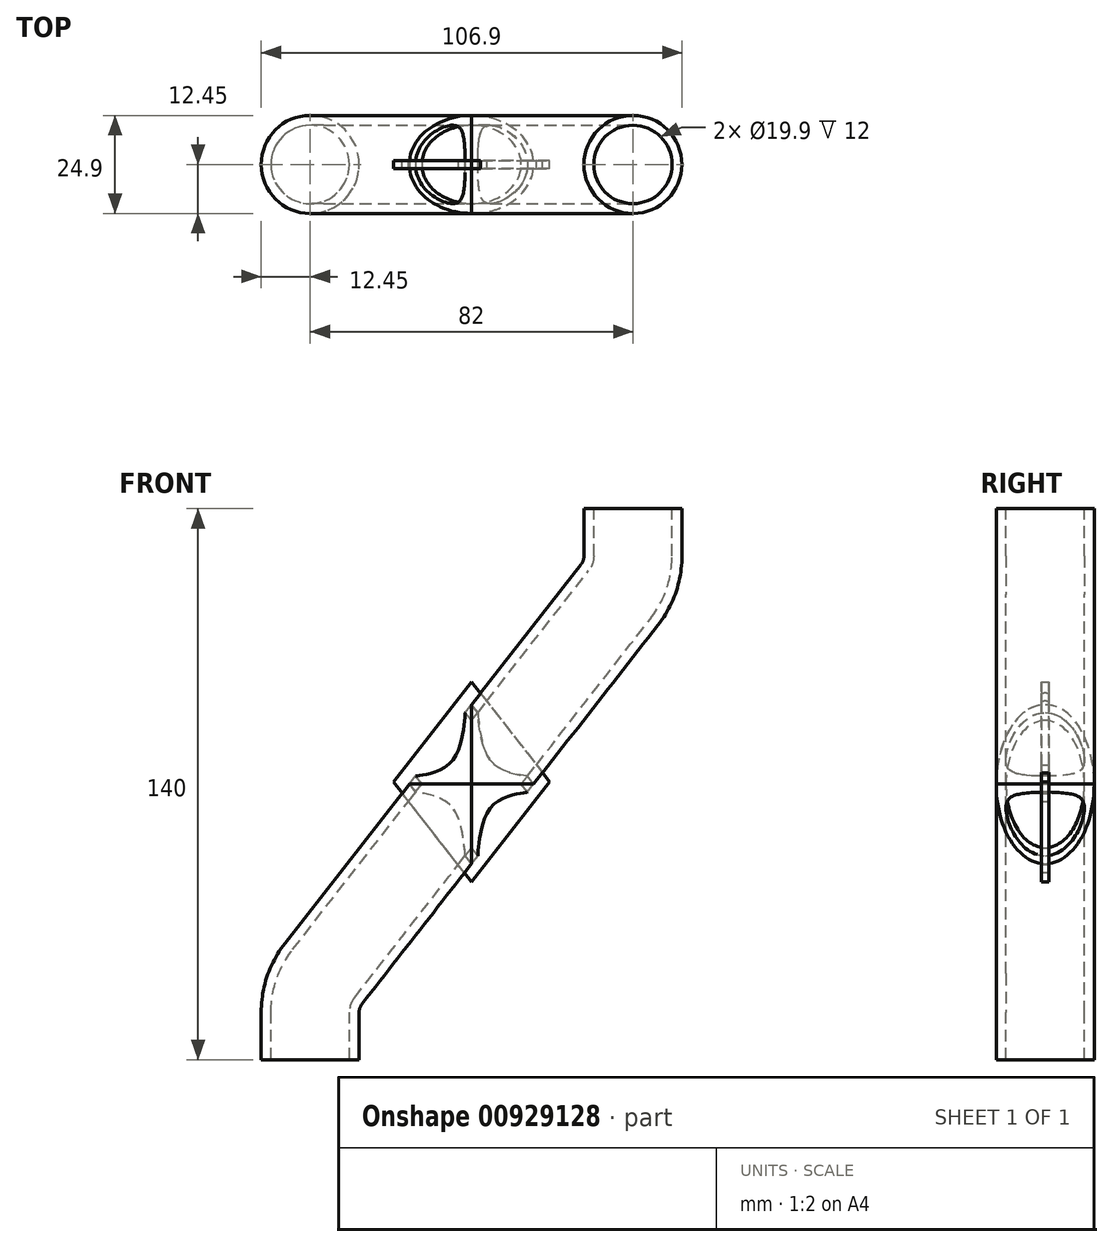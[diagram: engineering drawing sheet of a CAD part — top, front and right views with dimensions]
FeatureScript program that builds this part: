
annotation { "Feature Type Name" : "Feature", "Feature Type Description" : "" }
export const myFeature = defineFeature(function(context is Context, id is Id, definition is map)
    precondition{}
    {
        {
            var Q0;
            Q0=qCreatedBy(makeId("Front.planeOp"),FACE);
            var sketch = newSketch(context, id + "F0", { "sketchPlane" : qUnion([Q0])});
            skLineSegment(sketch, "E0", {"start": v(-41, 0) * mm, "end": v(-41, 12) * mm});
            skLineSegment(sketch, "E1", {"start": v(41, 0) * mm, "end": v(41, 12) * mm});
            skLineSegment(sketch, "E2", {"start": v(-37.6, 21.87) * mm, "end": v(37.6, 118.13) * mm});
            skLineSegment(sketch, "E3", {"start": v(37.6, 21.87) * mm, "end": v(0, 70) * mm});
            skLineSegment(sketch, "E4", {"start": v(-70.89, 0) * mm, "end": v(-70.89, 140) * mm});
            skLineSegment(sketch, "E5", {"start": v(41, 128) * mm, "end": v(41, 140) * mm});
            skPoint(sketch, "E6.visualSharp", {"position": v(-41, 17.52) * mm});
            skArc(sketch, "E6.filletArc", {"start": v(-37.6, 21.87) * mm, "mid": v(-40.13, 17.22) * mm, "end": v(-41, 12) * mm});
            skPoint(sketch, "E7.visualSharp", {"position": v(41, 17.52) * mm});
            skArc(sketch, "E7.filletArc", {"start": v(41, 12) * mm, "mid": v(40.13, 17.22) * mm, "end": v(37.6, 21.87) * mm});
            skPoint(sketch, "E8.visualSharp", {"position": v(41, 122.48) * mm});
            skArc(sketch, "E8.filletArc", {"start": v(37.6, 118.13) * mm, "mid": v(40.13, 122.78) * mm, "end": v(41, 128) * mm});
            skLineSegment(sketch, "E9", {"start": v(0, 70) * mm, "end": v(-15.6, 89.96) * mm});
            skSolve(sketch);
        }
        {
            var Q0;
            Q0=qCreatedBy(makeId("Top.planeOp"),FACE);
            var sketch = newSketch(context, id + "F1", { "sketchPlane" : qUnion([Q0])});
            skPoint(sketch, "E10.0", {"position": v(-41, 0) * mm});
            skCircle(sketch, "E11", {"center": v(-41, 0) * mm, "radius": 12.45 * mm});
            skCircle(sketch, "E12", {"center": v(41, 0) * mm, "radius": 12.45 * mm});
            skSolve(sketch);
        }
        {
            var Q0;
            Q0=makeQuery(id+"F1.imprint","IMPRINT",FACE,{"disambiguationData":[TD([[makeQuery(id+"F1.imprint","IMPRINT",EDGE,{"derivedFrom":sQuery(id+"F1.wireOp",EDGE,"E11")}),1.0]])]});
            var Q1;
            Q1=sQuery(id+"F0.wireOp",EDGE,"E0");
            var Q2;
            Q2=sQuery(id+"F0.wireOp",EDGE,"E6.filletArc");
            var Q3;
            Q3=sQuery(id+"F0.wireOp",EDGE,"E2");
            var Q4;
            Q4=sQuery(id+"F0.wireOp",EDGE,"E8.filletArc");
            var Q5;
            Q5=sQuery(id+"F0.wireOp",EDGE,"E5");
            sweep(context, id + "F2", {"profiles" : qUnion([Q0]), "path" : qUnion([Q1, Q2, Q3, Q4, Q5])});
        }
        {
            var Q0;
            Q0=makeQuery(id+"F1.imprint","IMPRINT",FACE,{"disambiguationData":[TD([[makeQuery(id+"F1.imprint","IMPRINT",EDGE,{"derivedFrom":sQuery(id+"F1.wireOp",EDGE,"E12")}),1.0]])]});
            var Q1;
            Q1=sQuery(id+"F0.wireOp",EDGE,"E1");
            var Q2;
            Q2=sQuery(id+"F0.wireOp",EDGE,"E7.filletArc");
            var Q3;
            Q3=sQuery(id+"F0.wireOp",EDGE,"E3");
            var Q4;
            Q4=sQuery(id+"F0.wireOp",EDGE,"E9");
            sweep(context, id + "F3", {"profiles" : qUnion([Q0]), "path" : qUnion([Q1, Q2, Q3, Q4])});
        }
        {
            var Q0;
            Q0=makeQuery(id+"F3.opSweep","CAP_FACE",FACE,{"disambiguationData":[OSD([sQuery(id+"F0.wireOp",VERTEX,"E9.end"),sQuery(id+"F1.wireOp",EDGE,"E12")])],"isStart":false});
            var Q1;
            Q1=makeQuery(id+"F2.opSweep","CAP_FACE",FACE,{"disambiguationData":[OSD([sQuery(id+"F0.wireOp",VERTEX,"E5.end"),sQuery(id+"F1.wireOp",EDGE,"E11")])],"isStart":false});
            var Q2;
            Q2=makeQuery(id+"F2.opSweep","CAP_FACE",FACE,{"disambiguationData":[OSD([sQuery(id+"F0.wireOp",VERTEX,"E0.start"),sQuery(id+"F1.wireOp",EDGE,"E11")])],"isStart":true});
            var Q3;
            Q3=makeQuery(id+"F3.opSweep","CAP_FACE",FACE,{"disambiguationData":[OSD([sQuery(id+"F0.wireOp",VERTEX,"E1.start"),sQuery(id+"F1.wireOp",EDGE,"E12")])],"isStart":true});
            shell(context, id + "F4", {"entities" : qUnion([Q0, Q1, Q2, Q3]), "thickness" : 2.5 * mm});
        }
        {
            var Q0;
            Q0=qCreatedBy(makeId("Front.planeOp"),FACE);
            var sketch = newSketch(context, id + "F5", { "sketchPlane" : qUnion([Q0])});
            skLineSegment(sketch, "E13", {"start": v(-25.4, 82.3) * mm, "end": v(27.79, 14.2) * mm});
            skLineSegment(sketch, "E14", {"start": v(47.41, 29.54) * mm, "end": v(-5.78, 97.63) * mm});
            skLineSegment(sketch, "E15", {"start": v(27.79, 125.8) * mm, "end": v(-47.41, 29.54) * mm});
            skLineSegment(sketch, "E16", {"start": v(-27.79, 14.2) * mm, "end": v(47.41, 110.46) * mm});
            skLineSegment(sketch, "E17", {"start": v(-19.86, 70.57) * mm, "end": v(0, 96) * mm});
            skLineSegment(sketch, "E18", {"start": v(0, 96) * mm, "end": v(19.86, 70.57) * mm});
            skLineSegment(sketch, "E19", {"start": v(19.86, 70.57) * mm, "end": v(0, 45.15) * mm});
            skLineSegment(sketch, "E20", {"start": v(0, 45.15) * mm, "end": v(-19.86, 70.57) * mm});
            skSolve(sketch);
        }
        {
            var Q0;
            {var subQ0=sQuery(id+"F5.wireOp",EDGE,"E17");var subQ1=sQuery(id+"F5.wireOp",EDGE,"E14");var subQ2=makeQuery(id+"F5.imprint","INTERSECT",VERTEX,{"derivedFrom":[subQ1,subQ0]});Q0=makeQuery(id+"F5.imprint","IMPRINT",FACE,{"disambiguationData":[TD([[makeQuery(id+"F5.imprint","IMPRINT",EDGE,{"disambiguationData":[TD([[subQ2,1.0]])],"derivedFrom":subQ1}),-1.0]])]});}
            var Q1;
            {var subQ0=sQuery(id+"F5.wireOp",EDGE,"E17");var subQ1=sQuery(id+"F5.wireOp",EDGE,"E13");var subQ2=makeQuery(id+"F5.imprint","INTERSECT",VERTEX,{"derivedFrom":[subQ1,subQ0]});Q1=makeQuery(id+"F5.imprint","IMPRINT",FACE,{"disambiguationData":[TD([[makeQuery(id+"F5.imprint","IMPRINT",EDGE,{"disambiguationData":[TD([[subQ2,-1.0]])],"derivedFrom":subQ1}),1.0]])]});}
            var Q2;
            {var subQ0=sQuery(id+"F5.wireOp",EDGE,"E16");var subQ1=sQuery(id+"F5.wireOp",EDGE,"E14");var subQ2=makeQuery(id+"F5.imprint","INTERSECT",VERTEX,{"derivedFrom":[subQ1,subQ0]});Q2=makeQuery(id+"F5.imprint","IMPRINT",FACE,{"disambiguationData":[TD([[makeQuery(id+"F5.imprint","IMPRINT",EDGE,{"disambiguationData":[TD([[subQ2,-1.0]])],"derivedFrom":subQ1}),-1.0]])]});}
            var Q3;
            {var subQ0=sQuery(id+"F5.wireOp",EDGE,"E15");var subQ1=sQuery(id+"F5.wireOp",EDGE,"E13");var subQ2=makeQuery(id+"F5.imprint","INTERSECT",VERTEX,{"derivedFrom":[subQ1,subQ0]});Q3=makeQuery(id+"F5.imprint","IMPRINT",FACE,{"disambiguationData":[TD([[makeQuery(id+"F5.imprint","IMPRINT",EDGE,{"disambiguationData":[TD([[subQ2,-1.0]])],"derivedFrom":subQ1}),1.0]])]});}
            var Q4;
            {var subQ0=sQuery(id+"F5.wireOp",EDGE,"E19");var subQ1=sQuery(id+"F5.wireOp",EDGE,"E14");var subQ2=makeQuery(id+"F5.imprint","INTERSECT",VERTEX,{"derivedFrom":[subQ1,subQ0]});Q4=makeQuery(id+"F5.imprint","IMPRINT",FACE,{"disambiguationData":[TD([[makeQuery(id+"F5.imprint","IMPRINT",EDGE,{"disambiguationData":[TD([[subQ2,-1.0]])],"derivedFrom":subQ1}),-1.0]])]});}
            var Q5;
            {var subQ0=sQuery(id+"F5.wireOp",EDGE,"E19");var subQ1=sQuery(id+"F5.wireOp",EDGE,"E13");var subQ2=makeQuery(id+"F5.imprint","INTERSECT",VERTEX,{"derivedFrom":[subQ1,subQ0]});Q5=makeQuery(id+"F5.imprint","IMPRINT",FACE,{"disambiguationData":[TD([[makeQuery(id+"F5.imprint","IMPRINT",EDGE,{"disambiguationData":[TD([[subQ2,1.0]])],"derivedFrom":subQ1}),1.0]])]});}
            var Q6;
            {var subQ0=sQuery(id+"F5.wireOp",EDGE,"E19");var subQ1=sQuery(id+"F5.wireOp",EDGE,"E13");var subQ2=makeQuery(id+"F5.imprint","INTERSECT",VERTEX,{"derivedFrom":[subQ1,subQ0]});Q6=makeQuery(id+"F5.imprint","IMPRINT",FACE,{"disambiguationData":[TD([[makeQuery(id+"F5.imprint","IMPRINT",EDGE,{"disambiguationData":[TD([[subQ2,1.0]])],"derivedFrom":subQ1}),-1.0]])]});}
            var Q7;
            {var subQ0=sQuery(id+"F5.wireOp",EDGE,"E15");var subQ1=sQuery(id+"F5.wireOp",EDGE,"E13");var subQ2=makeQuery(id+"F5.imprint","INTERSECT",VERTEX,{"derivedFrom":[subQ1,subQ0]});Q7=makeQuery(id+"F5.imprint","IMPRINT",FACE,{"disambiguationData":[TD([[makeQuery(id+"F5.imprint","IMPRINT",EDGE,{"disambiguationData":[TD([[subQ2,-1.0]])],"derivedFrom":subQ1}),-1.0]])]});}
            var Q8;
            {var subQ0=sQuery(id+"F5.wireOp",EDGE,"E17");var subQ1=sQuery(id+"F5.wireOp",EDGE,"E13");var subQ2=makeQuery(id+"F5.imprint","INTERSECT",VERTEX,{"derivedFrom":[subQ1,subQ0]});Q8=makeQuery(id+"F5.imprint","IMPRINT",FACE,{"disambiguationData":[TD([[makeQuery(id+"F5.imprint","IMPRINT",EDGE,{"disambiguationData":[TD([[subQ2,-1.0]])],"derivedFrom":subQ1}),-1.0]])]});}
            extrude(context, id + "F6", {"entities" : qUnion([Q0, Q1, Q2, Q3, Q4, Q5, Q6, Q7, Q8]), "endBound" : BoundingType.SYMMETRIC, "depth" : 2 * mm, "offsetDistance" : 25 * mm});
        }
        {
            var Q0;
            Q0=makeQuery(id+"F2.opSweep","SWEPT_BODY",BODY,{"disambiguationData":[OSD([sQuery(id+"F0.wireOp",EDGE,"E5"),sQuery(id+"F1.wireOp",EDGE,"E11")])]});
            var Q1;
            Q1=makeQuery(id+"F3.opSweep","SWEPT_BODY",BODY,{"disambiguationData":[OSD([sQuery(id+"F0.wireOp",EDGE,"E9"),sQuery(id+"F1.wireOp",EDGE,"E12")])]});
            booleanBodies(context, id + "F7", {"operationType" : BooleanOperationType.INTERSECTION, "tools" : qUnion([Q0, Q1]), "keepTools" : true});
        }
        {
            var Q0;
            Q0=makeQuery(id+"F7.opBoolean","INTERSECT",BODY,{"derivedFrom":[makeQuery(id+"F2.opSweep","SWEPT_BODY",BODY,{"disambiguationData":[OSD([sQuery(id+"F0.wireOp",EDGE,"E5"),sQuery(id+"F1.wireOp",EDGE,"E11")])]}),makeQuery(id+"F3.opSweep","SWEPT_BODY",BODY,{"disambiguationData":[OSD([sQuery(id+"F0.wireOp",EDGE,"E9"),sQuery(id+"F1.wireOp",EDGE,"E12")])]})]});
            var Q1;
            Q1=makeQuery(id+"F2.opSweep","SWEPT_BODY",BODY,{"disambiguationData":[OSD([sQuery(id+"F0.wireOp",EDGE,"E5"),sQuery(id+"F1.wireOp",EDGE,"E11")])]});
            var Q2;
            Q2=makeQuery(id+"F3.opSweep","SWEPT_BODY",BODY,{"disambiguationData":[OSD([sQuery(id+"F0.wireOp",EDGE,"E9"),sQuery(id+"F1.wireOp",EDGE,"E12")])]});
            booleanBodies(context, id + "F8", {"operationType" : BooleanOperationType.SUBTRACTION, "tools" : qUnion([Q0]), "targets" : qUnion([Q1, Q2]), "keepTools" : true});
        }
        {
            var Q0;
            Q0=makeQuery(id+"F8.opBoolean","SPLIT",BODY,{"disambiguationData":[OD(1.0)],"derivedFrom":makeQuery(id+"F3.opSweep","SWEPT_BODY",BODY,{"disambiguationData":[OSD([sQuery(id+"F0.wireOp",EDGE,"E9"),sQuery(id+"F1.wireOp",EDGE,"E12")])]})});
            var Q1;
            Q1=makeQuery(id+"F8.opBoolean","SPLIT",BODY,{"disambiguationData":[OD(3.0)],"derivedFrom":makeQuery(id+"F3.opSweep","SWEPT_BODY",BODY,{"disambiguationData":[OSD([sQuery(id+"F0.wireOp",EDGE,"E9"),sQuery(id+"F1.wireOp",EDGE,"E12")])]})});
            deleteBodies(context, id + "F9", {"entities" : qUnion([Q0, Q1])});
        }
        {
            var Q0;
            Q0=makeQuery(id+"F6.opExtrude","SWEPT_BODY",BODY,{"disambiguationData":[OSD([sQuery(id+"F5.wireOp",EDGE,"E17"),sQuery(id+"F5.wireOp",EDGE,"E18"),sQuery(id+"F5.wireOp",EDGE,"E19"),sQuery(id+"F5.wireOp",EDGE,"E20")])]});
            var Q1;
            Q1=makeQuery(id+"F8.opBoolean","SPLIT",BODY,{"disambiguationData":[OD(3.0)],"derivedFrom":makeQuery(id+"F2.opSweep","SWEPT_BODY",BODY,{"disambiguationData":[OSD([sQuery(id+"F0.wireOp",EDGE,"E5"),sQuery(id+"F1.wireOp",EDGE,"E11")])]})});
            booleanBodies(context, id + "F10", {"operationType" : BooleanOperationType.SUBTRACTION, "tools" : qUnion([Q0]), "targets" : qUnion([Q1]), "keepTools" : true});
        }
        {
            var Q0;
            Q0=makeQuery(id+"F10.opBoolean","SPLIT",BODY,{"disambiguationData":[OD(0.0)],"derivedFrom":makeQuery(id+"F8.opBoolean","SPLIT",BODY,{"disambiguationData":[OD(3.0)],"derivedFrom":makeQuery(id+"F2.opSweep","SWEPT_BODY",BODY,{"disambiguationData":[OSD([sQuery(id+"F0.wireOp",EDGE,"E5"),sQuery(id+"F1.wireOp",EDGE,"E11")])]})})});
            deleteBodies(context, id + "F11", {"entities" : qUnion([Q0])});
        }
    });
